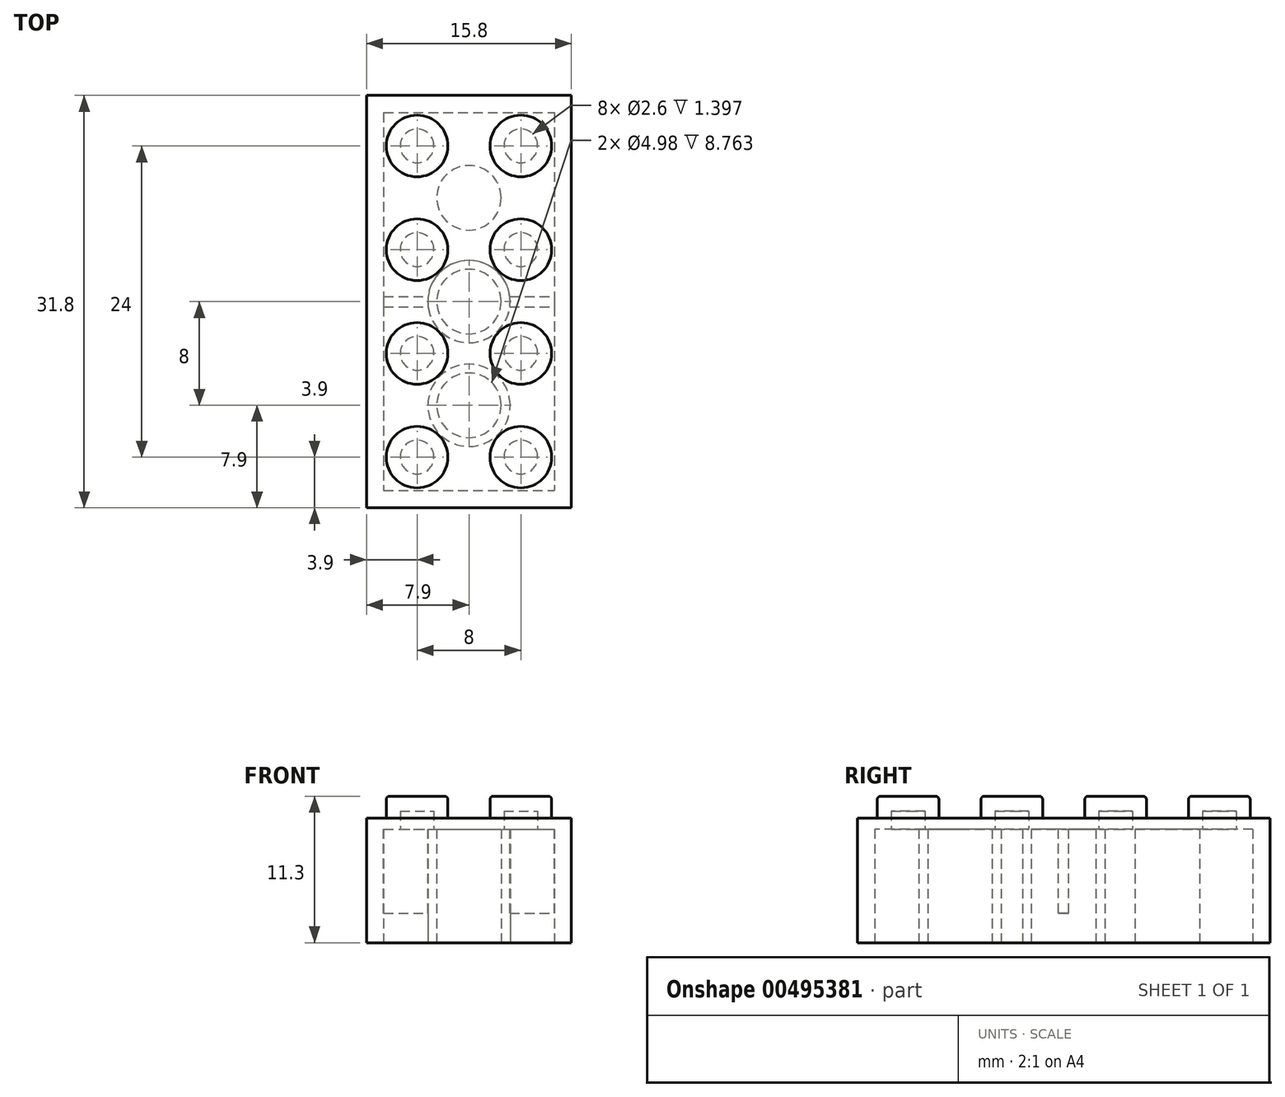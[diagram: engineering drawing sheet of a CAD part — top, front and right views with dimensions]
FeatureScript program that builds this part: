
annotation { "Feature Type Name" : "Feature", "Feature Type Description" : "" }
export const myFeature = defineFeature(function(context is Context, id is Id, definition is map)
    precondition{}
    {
        {
            var Q0;
            Q0=qCreatedBy(makeId("Top.planeOp"),FACE);
            var sketch = newSketch(context, id + "F0", { "sketchPlane" : qUnion([Q0])});
            skLineSegment(sketch, "E0.bottom", {"start": v(-15.8, -31.8) * mm, "end": v(0, -31.8) * mm});
            skLineSegment(sketch, "E0.top", {"start": v(-15.8, 0) * mm, "end": v(0, 0) * mm});
            skLineSegment(sketch, "E0.left", {"start": v(-15.8, -31.8) * mm, "end": v(-15.8, 0) * mm});
            skLineSegment(sketch, "E0.right", {"start": v(0, -31.8) * mm, "end": v(0, 0) * mm});
            skSolve(sketch);
        }
        {
            var Q0;
            Q0=makeQuery(id+"F0.imprint","IMPRINT",FACE,{"disambiguationData":[TD([[makeQuery(id+"F0.imprint","IMPRINT",EDGE,{"derivedFrom":sQuery(id+"F0.wireOp",EDGE,"E0.bottom")}),1.0]])]});
            extrude(context, id + "F1", {"entities" : qUnion([Q0]), "depth" : 9.6 * mm});
        }
        {
            var Q0;
            Q0=makeQuery(id+"F1.opExtrude","CAP_FACE",FACE,{"disambiguationData":[OSD([sQuery(id+"F0.wireOp",EDGE,"E0.bottom"),sQuery(id+"F0.wireOp",EDGE,"E0.top"),sQuery(id+"F0.wireOp",EDGE,"E0.left"),sQuery(id+"F0.wireOp",EDGE,"E0.right")])],"isStart":false});
            var sketch = newSketch(context, id + "F2", { "sketchPlane" : qUnion([Q0])});
            skCircle(sketch, "E1", {"center": v(-3.9, -3.9) * mm, "radius": 2.37 * mm});
            skCircle(sketch, "E2.0.1.0", {"center": v(-3.9, -11.9) * mm, "radius": 2.37 * mm});
            skCircle(sketch, "E2.0.2.0", {"center": v(-3.9, -19.9) * mm, "radius": 2.37 * mm});
            skCircle(sketch, "E2.0.3.0", {"center": v(-3.9, -27.9) * mm, "radius": 2.37 * mm});
            skCircle(sketch, "E2.1.0.0", {"center": v(-11.9, -3.9) * mm, "radius": 2.37 * mm});
            skCircle(sketch, "E2.1.1.0", {"center": v(-11.9, -11.9) * mm, "radius": 2.37 * mm});
            skCircle(sketch, "E2.1.2.0", {"center": v(-11.9, -19.9) * mm, "radius": 2.37 * mm});
            skCircle(sketch, "E2.1.3.0", {"center": v(-11.9, -27.9) * mm, "radius": 2.37 * mm});
            skLineSegment(sketch, "E2.direction1", {"start": v(-3.9, -3.9) * mm, "end": v(-11.9, -3.9) * mm, "construction": true});
            skLineSegment(sketch, "E2.direction2", {"start": v(-3.9, -3.9) * mm, "end": v(-3.9, -11.9) * mm, "construction": true});
            skSolve(sketch);
        }
        {
            var Q0;
            Q0=qSketchRegion(id+"F2",true);
            extrude(context, id + "F3", {"entities" : qUnion([Q0]), "operationType" : NewBodyOperationType.ADD, "depth" : 1.7 * mm});
        }
        {
            var Q0;
            Q0=makeQuery(id+"F1.opExtrude","CAP_FACE",FACE,{"disambiguationData":[OSD([sQuery(id+"F0.wireOp",EDGE,"E0.bottom"),sQuery(id+"F0.wireOp",EDGE,"E0.top"),sQuery(id+"F0.wireOp",EDGE,"E0.left"),sQuery(id+"F0.wireOp",EDGE,"E0.right")])],"isStart":true});
            var sketch = newSketch(context, id + "F4", { "sketchPlane" : qUnion([Q0])});
            skLineSegment(sketch, "E3.bottom", {"start": v(-14.48, 1.32) * mm, "end": v(-1.32, 1.32) * mm});
            skLineSegment(sketch, "E3.top", {"start": v(-14.48, 30.48) * mm, "end": v(-1.32, 30.48) * mm});
            skLineSegment(sketch, "E3.left", {"start": v(-14.48, 1.32) * mm, "end": v(-14.48, 30.48) * mm});
            skLineSegment(sketch, "E3.right", {"start": v(-1.32, 1.32) * mm, "end": v(-1.32, 30.48) * mm});
            skCircle(sketch, "E4", {"center": v(-7.9, 23.9) * mm, "radius": 3.18 * mm});
            skCircle(sketch, "E5", {"center": v(-7.9, 15.9) * mm, "radius": 3.18 * mm});
            skCircle(sketch, "E6", {"center": v(-7.9, 15.9) * mm, "radius": 2.49 * mm});
            skCircle(sketch, "E7", {"center": v(-7.9, 23.9) * mm, "radius": 2.49 * mm});
            skLineSegment(sketch, "E8", {"start": v(-7.9, 1.32) * mm, "end": v(-7.9, 30.48) * mm, "construction": true});
            skLineSegment(sketch, "E9", {"start": v(-1.32, 15.9) * mm, "end": v(-14.48, 15.9) * mm, "construction": true});
            skLineSegment(sketch, "E10", {"start": v(-3.9, 27.9) * mm, "end": v(-11.9, 19.9) * mm, "construction": true});
            skCircle(sketch, "E11.MirrorC", {"center": v(-7.9, 7.9) * mm, "radius": 3.18 * mm});
            skCircle(sketch, "E12.MirrorC", {"center": v(-7.9, 7.9) * mm, "radius": 2.49 * mm});
            skSolve(sketch);
        }
        {
            var Q0;
            Q0=qSketchRegion(id+"F4",true);
            extrude(context, id + "F5", {"entities" : qUnion([Q0]), "operationType" : NewBodyOperationType.REMOVE, "oppositeDirection" : true, "depth" : 8.76 * mm});
        }
        {
            var Q0;
            Q0=makeQuery(id+"F4.imprint","IMPRINT",FACE,{"disambiguationData":[TD([[makeQuery(id+"F4.imprint","IMPRINT",EDGE,{"derivedFrom":sQuery(id+"F4.wireOp",EDGE,"E7")}),1.0]])]});
            var Q1;
            Q1=makeQuery(id+"F4.imprint","IMPRINT",FACE,{"disambiguationData":[TD([[makeQuery(id+"F4.imprint","IMPRINT",EDGE,{"derivedFrom":sQuery(id+"F4.wireOp",EDGE,"E6")}),1.0]])]});
            var Q2;
            Q2=makeQuery(id+"F4.imprint","IMPRINT",FACE,{"disambiguationData":[TD([[makeQuery(id+"F4.imprint","IMPRINT",EDGE,{"derivedFrom":sQuery(id+"F4.wireOp",EDGE,"ewNiTv9N-kwH8-zp8D-8VmK-iinGs2Req3qf")}),1.0]])]});
            var Q3;
            Q3=makeQuery(id+"F4.imprint","IMPRINT",FACE,{"disambiguationData":[TD([[makeQuery(id+"F4.imprint","IMPRINT",EDGE,{"derivedFrom":sQuery(id+"F4.wireOp",EDGE,"E12.MirrorC")}),-1.0]])]});
            extrude(context, id + "F6", {"entities" : qUnion([Q0, Q1, Q2, Q3]), "operationType" : NewBodyOperationType.REMOVE, "oppositeDirection" : true, "depth" : 8.76 * mm});
        }
        {
            var Q0;
            Q0=makeQuery(id+"F5.boolean.opBoolean","COPY",FACE,{"derivedFrom":makeQuery(id+"F5.opExtrude","CAP_FACE",FACE,{"disambiguationData":[OSD([sQuery(id+"F4.wireOp",EDGE,"E3.bottom"),sQuery(id+"F4.wireOp",EDGE,"E3.top"),sQuery(id+"F4.wireOp",EDGE,"E3.left"),sQuery(id+"F4.wireOp",EDGE,"E3.right"),sQuery(id+"F4.wireOp",EDGE,"E4"),sQuery(id+"F4.wireOp",EDGE,"E5"),sQuery(id+"F4.wireOp",EDGE,"eTSD7xsl-GOij-G5rq-uAMM-qAvroOvZzWVF")])],"isStart":false})});
            var sketch = newSketch(context, id + "F7", { "sketchPlane" : qUnion([Q0])});
            skLineSegment(sketch, "E13", {"start": v(-14.48, 15.9) * mm, "end": v(-1.32, 15.9) * mm, "construction": true});
            skLineSegment(sketch, "E14.bottom", {"start": v(-14.48, 16.3) * mm, "end": v(-10.76, 16.3) * mm});
            skLineSegment(sketch, "E14.top", {"start": v(-14.48, 15.5) * mm, "end": v(-10.76, 15.5) * mm});
            skLineSegment(sketch, "E14.left", {"start": v(-14.48, 16.3) * mm, "end": v(-14.48, 15.5) * mm});
            skLineSegment(sketch, "E14.right", {"start": v(-10.76, 16.3) * mm, "end": v(-10.76, 15.5) * mm});
            skLineSegment(sketch, "E15.bottom", {"start": v(-5.03, 16.3) * mm, "end": v(-1.32, 16.3) * mm});
            skLineSegment(sketch, "E15.top", {"start": v(-5.03, 15.5) * mm, "end": v(-1.32, 15.5) * mm});
            skLineSegment(sketch, "E15.left", {"start": v(-5.03, 16.3) * mm, "end": v(-5.03, 15.5) * mm});
            skLineSegment(sketch, "E15.right", {"start": v(-1.32, 16.3) * mm, "end": v(-1.32, 15.5) * mm});
            skSolve(sketch);
        }
        {
            var Q0;
            {var subQ0=sQuery(id+"F7.wireOp",EDGE,"E15.right");Q0=makeQuery(id+"F7.imprint","IMPRINT",FACE,{"disambiguationData":[TD([[makeQuery(id+"F7.imprint","IMPRINT",EDGE,{"derivedFrom":subQ0}),1.0]])]});}
            var Q1;
            {var subQ0=sQuery(id+"F7.wireOp",EDGE,"E14.left");Q1=makeQuery(id+"F7.imprint","IMPRINT",FACE,{"disambiguationData":[TD([[makeQuery(id+"F7.imprint","IMPRINT",EDGE,{"derivedFrom":subQ0}),-1.0]])]});}
            var Q2;
            {var subQ0=sQuery(id+"F0.wireOp",EDGE,"E0.left");var subQ1=sQuery(id+"F0.wireOp",EDGE,"E0.top");var subQ2=sQuery(id+"F0.wireOp",EDGE,"E0.right");var subQ3=sQuery(id+"F0.wireOp",EDGE,"E0.bottom");Q2=makeQuery(id+"F5.boolean.opBoolean","SPLIT",FACE,{"disambiguationData":[TD([makeQuery(id+"F1.opExtrude","SWEPT_FACE",FACE,{"disambiguationData":[OSD([subQ3])]})])],"derivedFrom":makeQuery(id+"F1.opExtrude","CAP_FACE",FACE,{"disambiguationData":[OSD([subQ3,subQ1,subQ0,subQ2])],"isStart":true})});}
            extrude(context, id + "F8", {"entities" : qUnion([Q0, Q1]), "operationType" : NewBodyOperationType.ADD, "endBoundEntityFace" : qUnion([Q2]), "depth" : 6.48 * mm});
        }
        {
            var Q0;
            {var subQ0=sQuery(id+"F4.wireOp",EDGE,"E4");var subQ1=sQuery(id+"F4.wireOp",EDGE,"E3.right");var subQ2=sQuery(id+"F4.wireOp",EDGE,"E3.left");var subQ3=sQuery(id+"F4.wireOp",EDGE,"E3.top");var subQ4=sQuery(id+"F4.wireOp",EDGE,"E5");Q0=makeQuery(id+"F8.boolean.opBoolean","SPLIT",FACE,{"disambiguationData":[TD([makeQuery(id+"F5.boolean.opBoolean","COPY",FACE,{"derivedFrom":makeQuery(id+"F5.opExtrude","SWEPT_FACE",FACE,{"disambiguationData":[OSD([subQ3])]})})])],"derivedFrom":makeQuery(id+"F5.boolean.opBoolean","COPY",FACE,{"derivedFrom":makeQuery(id+"F5.opExtrude","CAP_FACE",FACE,{"disambiguationData":[OSD([sQuery(id+"F4.wireOp",EDGE,"E3.bottom"),subQ3,subQ2,subQ1,subQ0,subQ4,sQuery(id+"F4.wireOp",EDGE,"eTSD7xsl-GOij-G5rq-uAMM-qAvroOvZzWVF")])],"isStart":false})})});}
            var sketch = newSketch(context, id + "F9", { "sketchPlane" : qUnion([Q0])});
            skCircle(sketch, "E16", {"center": v(-11.9, 3.9) * mm, "radius": 1.3 * mm});
            skCircle(sketch, "E17.0.1.0", {"center": v(-11.9, 11.9) * mm, "radius": 1.3 * mm});
            skCircle(sketch, "E17.0.2.0", {"center": v(-11.9, 19.9) * mm, "radius": 1.3 * mm});
            skCircle(sketch, "E17.0.3.0", {"center": v(-11.9, 27.9) * mm, "radius": 1.3 * mm});
            skCircle(sketch, "E17.1.0.0", {"center": v(-3.9, 3.9) * mm, "radius": 1.3 * mm});
            skCircle(sketch, "E17.1.1.0", {"center": v(-3.9, 11.9) * mm, "radius": 1.3 * mm});
            skCircle(sketch, "E17.1.2.0", {"center": v(-3.9, 19.9) * mm, "radius": 1.3 * mm});
            skCircle(sketch, "E17.1.3.0", {"center": v(-3.9, 27.9) * mm, "radius": 1.3 * mm});
            skLineSegment(sketch, "E17.direction1", {"start": v(-11.9, 3.9) * mm, "end": v(-3.9, 3.9) * mm, "construction": true});
            skLineSegment(sketch, "E17.direction2", {"start": v(-11.9, 3.9) * mm, "end": v(-11.9, 11.9) * mm, "construction": true});
            skSolve(sketch);
        }
        {
            var Q0;
            Q0=qSketchRegion(id+"F9",true);
            extrude(context, id + "F10", {"entities" : qUnion([Q0]), "operationType" : NewBodyOperationType.REMOVE, "oppositeDirection" : true, "depth" : 1.4 * mm});
        }
        {
            var Q0;
            Q0=makeQuery(id+"F3.opExtrude","CAP_EDGE",EDGE,{"disambiguationData":[OSD([sQuery(id+"F2.wireOp",EDGE,"E2.1.0.0")])],"isStart":false});
            var Q1;
            Q1=makeQuery(id+"F3.opExtrude","CAP_EDGE",EDGE,{"disambiguationData":[OSD([sQuery(id+"F2.wireOp",EDGE,"E1")])],"isStart":false});
            var Q2;
            Q2=makeQuery(id+"F3.opExtrude","CAP_EDGE",EDGE,{"disambiguationData":[OSD([sQuery(id+"F2.wireOp",EDGE,"E2.1.1.0")])],"isStart":false});
            var Q3;
            Q3=makeQuery(id+"F3.opExtrude","CAP_EDGE",EDGE,{"disambiguationData":[OSD([sQuery(id+"F2.wireOp",EDGE,"E2.1.2.0")])],"isStart":false});
            var Q4;
            Q4=makeQuery(id+"F3.opExtrude","CAP_EDGE",EDGE,{"disambiguationData":[OSD([sQuery(id+"F2.wireOp",EDGE,"E2.0.1.0")])],"isStart":false});
            var Q5;
            Q5=makeQuery(id+"F3.opExtrude","CAP_EDGE",EDGE,{"disambiguationData":[OSD([sQuery(id+"F2.wireOp",EDGE,"E2.0.2.0")])],"isStart":false});
            var Q6;
            Q6=makeQuery(id+"F3.opExtrude","CAP_EDGE",EDGE,{"disambiguationData":[OSD([sQuery(id+"F2.wireOp",EDGE,"E2.1.3.0")])],"isStart":false});
            var Q7;
            Q7=makeQuery(id+"F3.opExtrude","CAP_EDGE",EDGE,{"disambiguationData":[OSD([sQuery(id+"F2.wireOp",EDGE,"E2.0.3.0")])],"isStart":false});
            fillet(context, id + "F11", {"entities" : qUnion([Q0, Q1, Q2, Q3, Q4, Q5, Q6, Q7]), "radius" : 0.25 * mm, "tangentPropagation" : true, "allowEdgeOverflow" : false});
        }
    });
